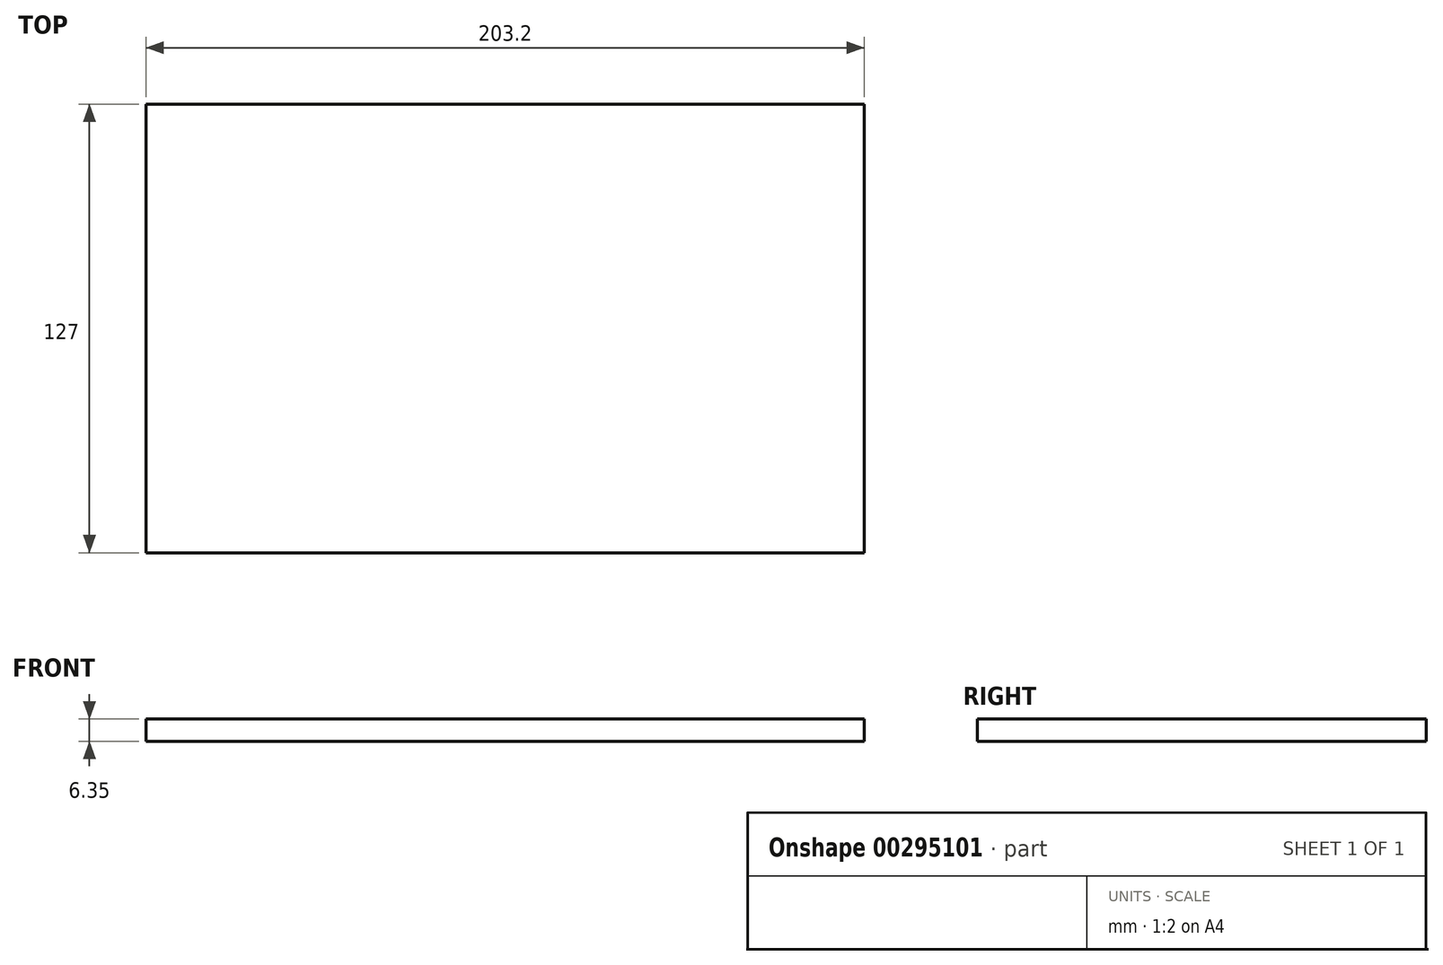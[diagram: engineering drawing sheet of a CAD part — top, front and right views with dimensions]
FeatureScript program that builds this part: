
annotation { "Feature Type Name" : "Feature", "Feature Type Description" : "" }
export const myFeature = defineFeature(function(context is Context, id is Id, definition is map)
    precondition{}
    {
        {
            var Q0;
            Q0=qCreatedBy(makeId("Top.planeOp"),FACE);
            var sketch = newSketch(context, id + "F0", { "sketchPlane" : qUnion([Q0])});
            skLineSegment(sketch, "E0.bottom", {"start": v(-99.47, 50.4) * mm, "end": v(103.73, 50.4) * mm});
            skLineSegment(sketch, "E0.top", {"start": v(-99.47, -76.6) * mm, "end": v(103.73, -76.6) * mm});
            skLineSegment(sketch, "E0.left", {"start": v(-99.47, 50.4) * mm, "end": v(-99.47, -76.6) * mm});
            skLineSegment(sketch, "E0.right", {"start": v(103.73, 50.4) * mm, "end": v(103.73, -76.6) * mm});
            skSolve(sketch);
        }
        {
            var Q0;
            Q0 = qSketchRegion(id + "F0", true);
            extrude(context, id + "F1", {"entities" : qUnion([Q0]), "depth" : 6.35 * mm});
        }
    });
